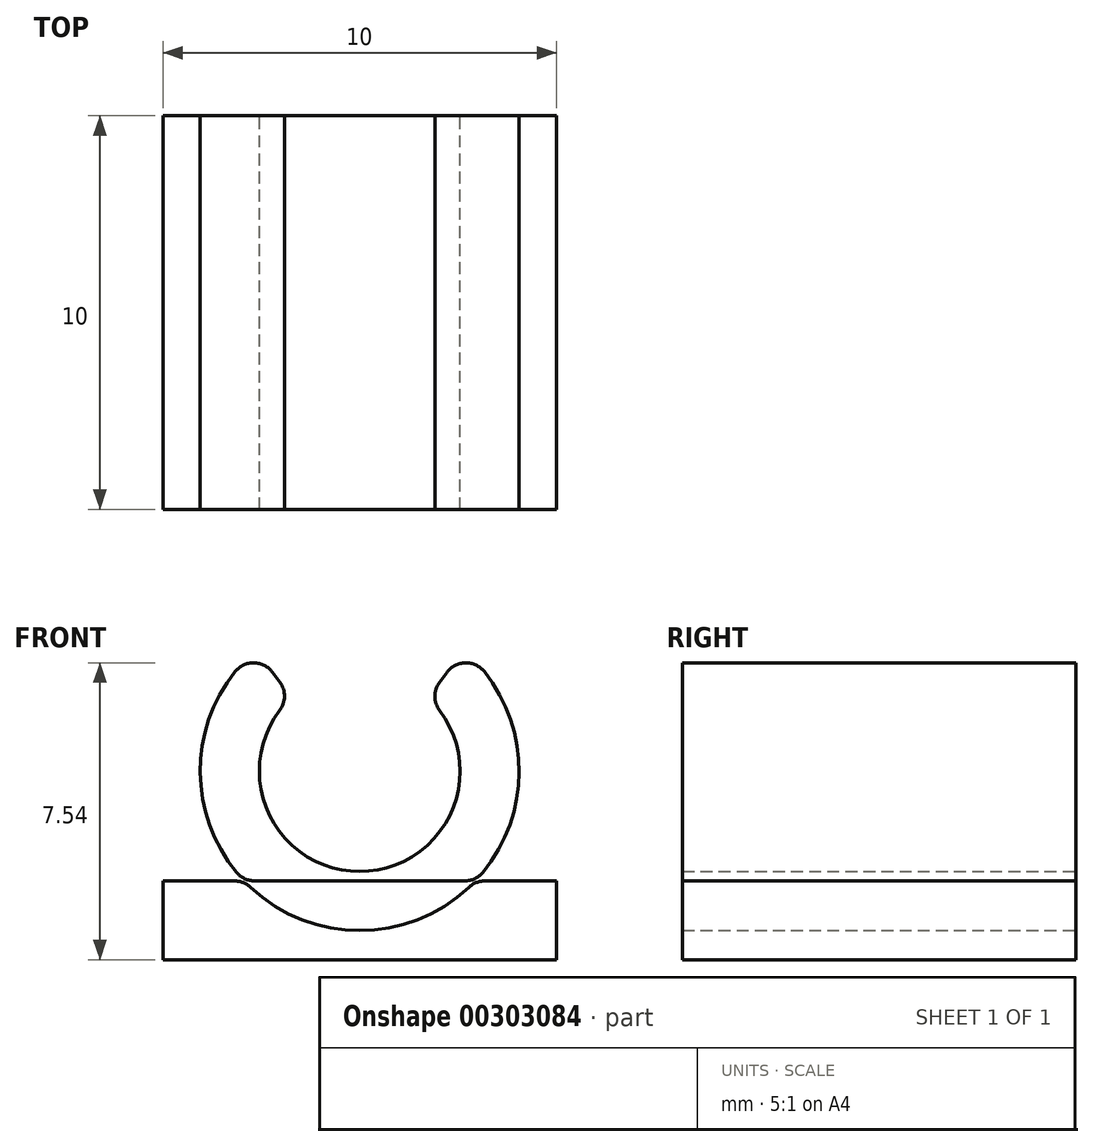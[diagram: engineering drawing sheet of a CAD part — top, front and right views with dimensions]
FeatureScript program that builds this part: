
annotation { "Feature Type Name" : "Feature", "Feature Type Description" : "" }
export const myFeature = defineFeature(function(context is Context, id is Id, definition is map)
    precondition{}
    {
        {
            var Q0;
            Q0=qCreatedBy(makeId("Front.planeOp"),FACE);
            var sketch = newSketch(context, id + "F0", { "sketchPlane" : qUnion([Q0])});
            skLineSegment(sketch, "E0.bottom", {"start": v(-5, 2) * mm, "end": v(5, 2) * mm});
            skLineSegment(sketch, "E0.top", {"start": v(-5, 0) * mm, "end": v(5, 0) * mm});
            skLineSegment(sketch, "E0.left", {"start": v(-5, 2) * mm, "end": v(-5, 0) * mm});
            skLineSegment(sketch, "E0.right", {"start": v(5, 2) * mm, "end": v(5, 0) * mm});
            skCircle(sketch, "E1", {"center": v(0, 4.8) * mm, "radius": 2.55 * mm});
            skCircle(sketch, "E2.0", {"center": v(0, 4.8) * mm, "radius": 4.05 * mm});
            skLineSegment(sketch, "E3", {"start": v(1.74, 6.66) * mm, "end": v(2.63, 7.87) * mm});
            skLineSegment(sketch, "E4", {"start": v(-1.74, 6.66) * mm, "end": v(-2.63, 7.87) * mm});
            skPoint(sketch, "E5", {"position": v(-2.93, 2) * mm});
            skPoint(sketch, "E6", {"position": v(2.93, 2) * mm});
            skSolve(sketch);
        }
        {
            var Q0;
            {var subQ0=sQuery(id+"F0.wireOp",EDGE,"E2.0");var subQ1=sQuery(id+"F0.wireOp",EDGE,"E0.bottom");var subQ2=makeQuery(id+"F0.imprint","INTERSECT",VERTEX,{"disambiguationData":[OD(0.0)],"derivedFrom":[subQ1,subQ0]});Q0=makeQuery(id+"F0.imprint","IMPRINT",FACE,{"disambiguationData":[TD([[makeQuery(id+"F0.imprint","IMPRINT",EDGE,{"disambiguationData":[TD([[subQ2,-1.0]])],"derivedFrom":subQ1}),-1.0]])]});}
            var Q1;
            Q1=makeQuery(id+"F0.imprint","IMPRINT",FACE,{"disambiguationData":[TD([[makeQuery(id+"F0.imprint","IMPRINT",EDGE,{"derivedFrom":sQuery(id+"F0.wireOp",EDGE,"E0.top")}),1.0]])]});
            var Q2;
            {var subQ4=sQuery(id+"F0.wireOp",EDGE,"E3");Q2=makeQuery(id+"F0.imprint","IMPRINT",FACE,{"disambiguationData":[TD([[makeQuery(id+"F0.imprint","IMPRINT",EDGE,{"derivedFrom":subQ4}),-1.0]])]});}
            extrude(context, id + "F1", {"entities" : qUnion([Q0, Q1, Q2]), "depth" : 10 * mm});
        }
        {
            var Q0;
            Q0=makeQuery(id+"F1.opExtrude","SWEPT_EDGE",EDGE,{"disambiguationData":[OSD([sQuery(id+"F0.wireOp",EDGE,"E1"),sQuery(id+"F0.wireOp",EDGE,"E3")])]});
            var Q1;
            Q1=makeQuery(id+"F1.opExtrude","SWEPT_EDGE",EDGE,{"disambiguationData":[OSD([sQuery(id+"F0.wireOp",EDGE,"E1"),sQuery(id+"F0.wireOp",EDGE,"E4")])]});
            var Q2;
            Q2=makeQuery(id+"F1.opExtrude","SWEPT_EDGE",EDGE,{"disambiguationData":[OSD([sQuery(id+"F0.wireOp",EDGE,"E2.0"),sQuery(id+"F0.wireOp",EDGE,"E4")])]});
            var Q3;
            Q3=makeQuery(id+"F1.opExtrude","SWEPT_EDGE",EDGE,{"disambiguationData":[OSD([sQuery(id+"F0.wireOp",EDGE,"E2.0"),sQuery(id+"F0.wireOp",EDGE,"E3")])]});
            fillet(context, id + "F2", {"entities" : qUnion([Q0, Q1, Q2, Q3]), "radius" : .6 * mm, "tangentPropagation" : true, "allowEdgeOverflow" : false});
        }
        {
            var Q0;
            {var subQ0=sQuery(id+"F0.wireOp",EDGE,"E2.0");var subQ1=sQuery(id+"F0.wireOp",EDGE,"E0.bottom");Q0=makeQuery(id+"F1.opExtrude","SWEPT_EDGE",EDGE,{"disambiguationData":[OSD([subQ1,subQ0]),TDD([makeQuery(id+"F0.imprint","INTERSECT",VERTEX,{"disambiguationData":[OD(1.0)],"derivedFrom":[subQ1,subQ0]})])]});}
            var Q1;
            {var subQ0=sQuery(id+"F0.wireOp",EDGE,"E2.0");var subQ1=sQuery(id+"F0.wireOp",EDGE,"E0.bottom");Q1=makeQuery(id+"F1.opExtrude","SWEPT_EDGE",EDGE,{"disambiguationData":[OSD([subQ1,subQ0]),TDD([makeQuery(id+"F0.imprint","INTERSECT",VERTEX,{"disambiguationData":[OD(0.0)],"derivedFrom":[subQ1,subQ0]})])]});}
            fillet(context, id + "F3", {"entities" : qUnion([Q0, Q1]), "radius" : .6 * mm, "tangentPropagation" : true, "allowEdgeOverflow" : false});
        }
    });
